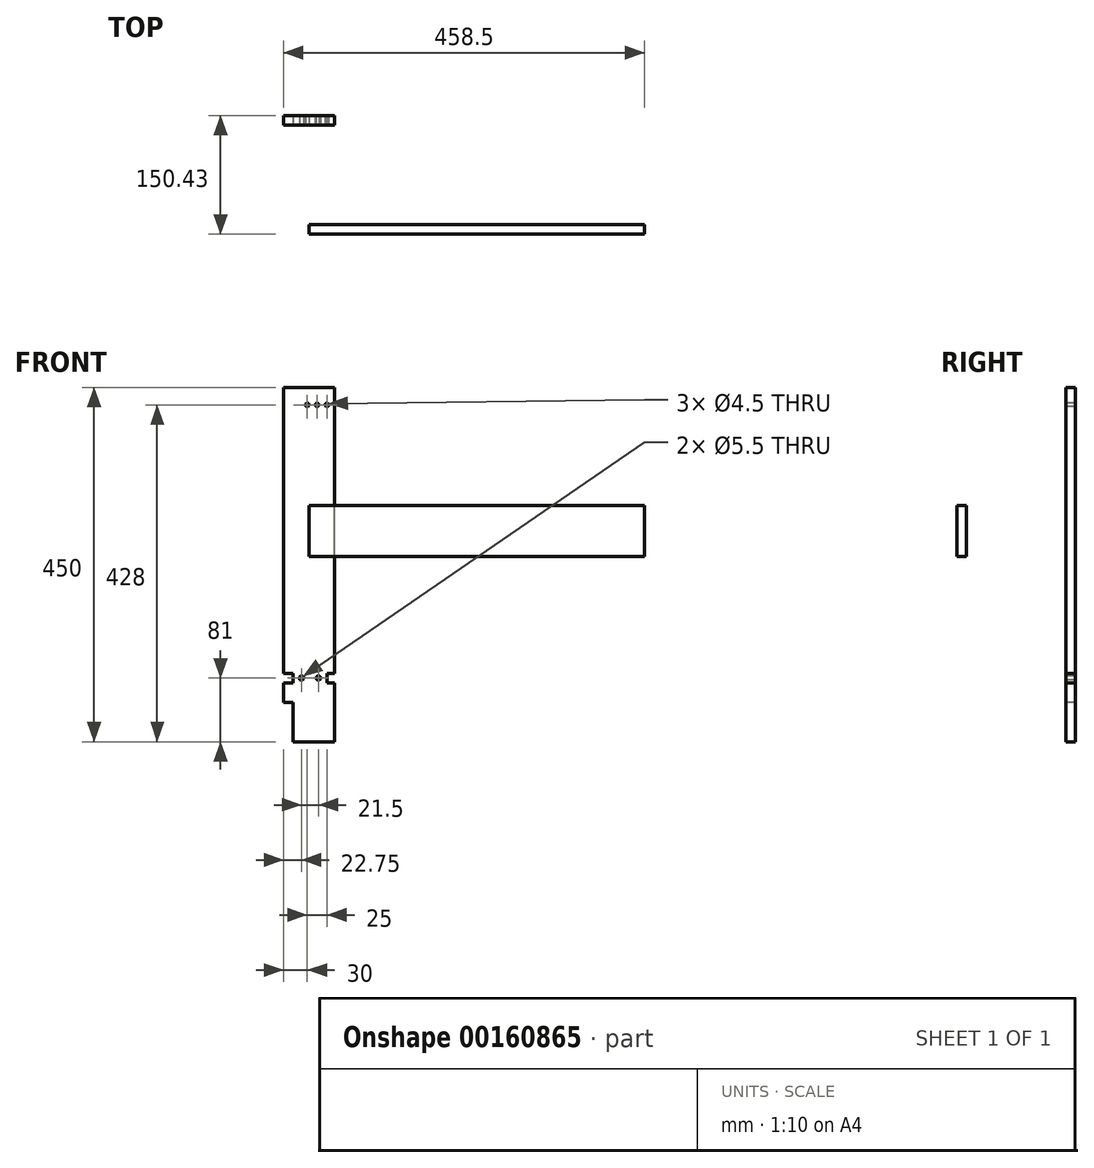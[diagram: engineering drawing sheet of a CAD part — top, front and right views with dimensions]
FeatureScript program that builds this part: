
annotation { "Feature Type Name" : "Feature", "Feature Type Description" : "" }
export const myFeature = defineFeature(function(context is Context, id is Id, definition is map)
    precondition{}
    {
        {
            var Q0;
            Q0=qCreatedBy(makeId("Front.planeOp"),FACE);
            var sketch = newSketch(context, id + "F0", { "sketchPlane" : qUnion([Q0])});
            skLineSegment(sketch, "E0.bottom", {"start": v(-32.5, 225) * mm, "end": v(32.5, 225) * mm});
            skLineSegment(sketch, "E1", {"start": v(32.5, -225) * mm, "end": v(-20.5, -225) * mm});
            skLineSegment(sketch, "E2", {"start": v(-32.5, -138) * mm, "end": v(-32.5, 225) * mm});
            skLineSegment(sketch, "E3", {"start": v(22.5, -138) * mm, "end": v(22.5, -150) * mm});
            skLineSegment(sketch, "E4", {"start": v(22.5, -150) * mm, "end": v(-20.5, -150) * mm, "construction": true});
            skLineSegment(sketch, "E5", {"start": v(22.5, -150) * mm, "end": v(32.5, -150) * mm});
            skLineSegment(sketch, "E6", {"start": v(22.5, -138) * mm, "end": v(32.5, -138) * mm});
            skLineSegment(sketch, "E7", {"start": v(-20.5, -150) * mm, "end": v(-20.5, -138) * mm});
            skLineSegment(sketch, "E8", {"start": v(32.5, -225) * mm, "end": v(32.5, -150) * mm});
            skLineSegment(sketch, "E9", {"start": v(32.5, -138) * mm, "end": v(32.5, 225) * mm});
            skCircle(sketch, "E10", {"center": v(11.75, -144) * mm, "radius": 2.75 * mm});
            skPoint(sketch, "E11", {"position": v(22.5, -144) * mm});
            skLineSegment(sketch, "E12", {"start": v(-20.5, -138) * mm, "end": v(22.5, -138) * mm, "construction": true});
            skLineSegment(sketch, "E13", {"start": v(-20.5, -138) * mm, "end": v(-32.5, -138) * mm});
            skLineSegment(sketch, "E14", {"start": v(-20.5, -150) * mm, "end": v(-32.5, -150) * mm});
            skLineSegment(sketch, "E15", {"start": v(-32.5, -150) * mm, "end": v(-32.5, -175) * mm});
            skLineSegment(sketch, "E16", {"start": v(-20.5, -225) * mm, "end": v(-20.5, -175) * mm});
            skLineSegment(sketch, "E17", {"start": v(-20.5, -175) * mm, "end": v(-32.5, -175) * mm});
            skCircle(sketch, "E18.1.0.0", {"center": v(-9.75, -144) * mm, "radius": 2.75 * mm});
            skLineSegment(sketch, "E18.direction1", {"start": v(11.75, -144) * mm, "end": v(-9.75, -144) * mm, "construction": true});
            skPoint(sketch, "E19", {"position": v(42.5, -143) * mm});
            skPoint(sketch, "E20", {"position": v(41.3, 207) * mm});
            skLineSegment(sketch, "E21", {"start": v(32.5, 207) * mm, "end": v(-12.5, 207) * mm, "construction": true});
            skLineSegment(sketch, "E22", {"start": v(32.5, 199) * mm, "end": v(-12.5, 199) * mm, "construction": true});
            skCircle(sketch, "E23", {"center": v(22.5, 203) * mm, "radius": 2.25 * mm});
            skCircle(sketch, "E24", {"center": v(10, 203) * mm, "radius": 2.25 * mm});
            skCircle(sketch, "E25", {"center": v(-2.5, 203) * mm, "radius": 2.25 * mm});
            skLineSegment(sketch, "E26", {"start": v(-12.5, 207) * mm, "end": v(-12.5, 199) * mm, "construction": true});
            skPoint(sketch, "E27", {"position": v(-12.5, 203) * mm});
            skSolve(sketch);
        }
        {
            var Q0;
            Q0 = qSketchRegion(id + "F0", true);
            extrude(context, id + "F1", {"entities" : qUnion([Q0]), "oppositeDirection" : true, "depth" : 12 * mm});
        }
        {
            var Q0;
            Q0=qCreatedBy(makeId("Right.planeOp"),FACE);
            var sketch = newSketch(context, id + "F2", { "sketchPlane" : qUnion([Q0])});
            skLineSegment(sketch, "E28.bottom", {"start": v(-126.43, 10.38) * mm, "end": v(-138.43, 10.38) * mm});
            skLineSegment(sketch, "E28.top", {"start": v(-126.43, 75.38) * mm, "end": v(-138.43, 75.38) * mm});
            skLineSegment(sketch, "E28.left", {"start": v(-126.43, 10.38) * mm, "end": v(-126.43, 75.38) * mm});
            skLineSegment(sketch, "E28.right", {"start": v(-138.43, 10.38) * mm, "end": v(-138.43, 75.38) * mm});
            skSolve(sketch);
        }
        {
            var Q0;
            Q0 = qSketchRegion(id + "F2", true);
            extrude(context, id + "F3", {"entities" : qUnion([Q0]), "depth" : 426 * mm});
        }
    });
